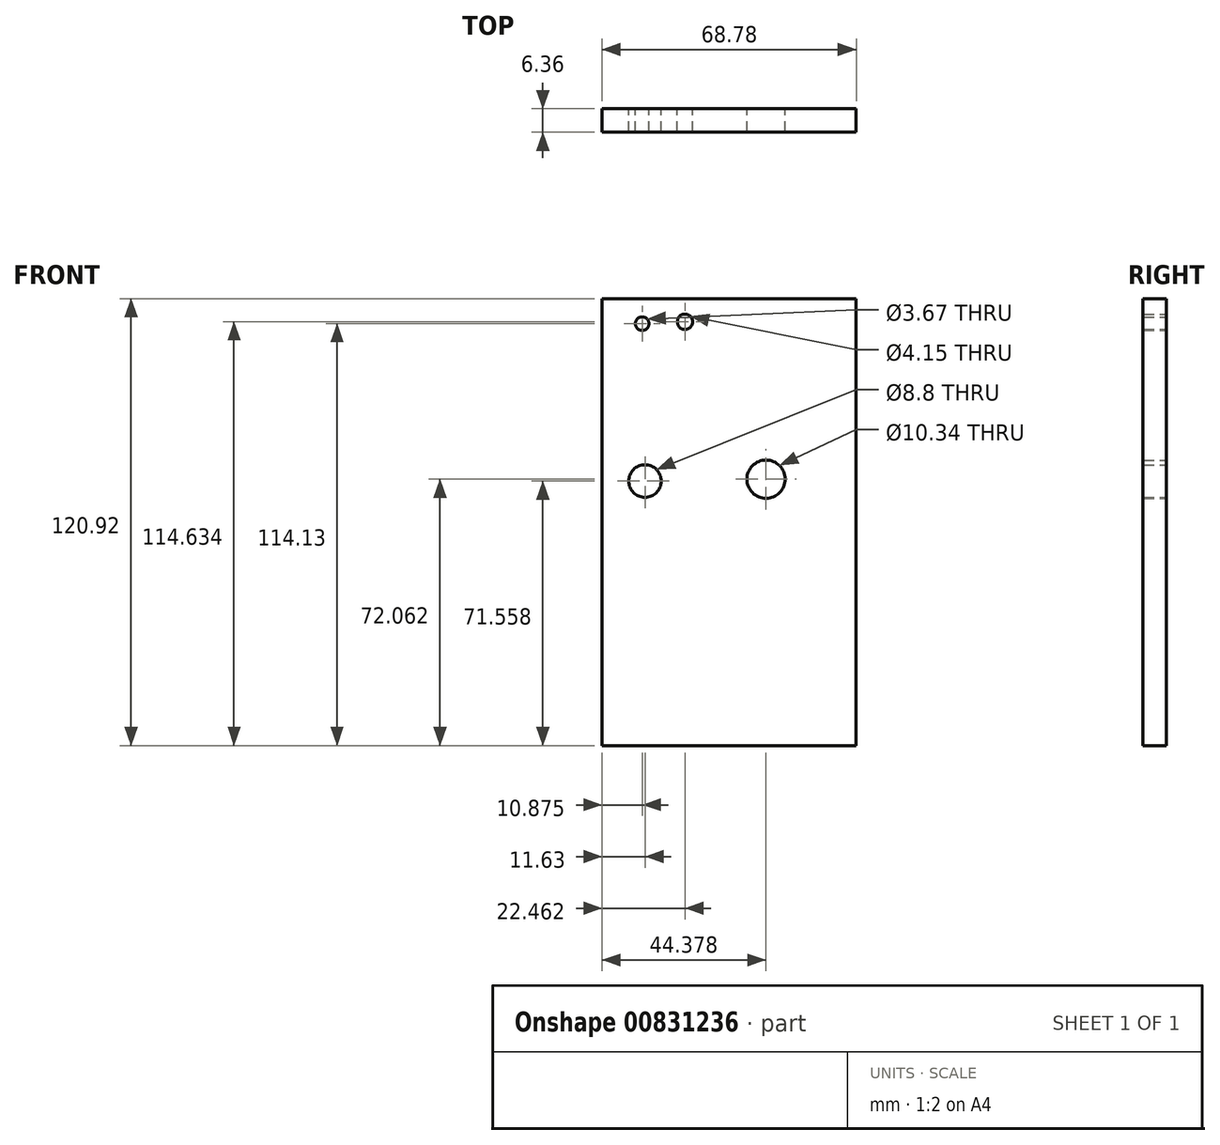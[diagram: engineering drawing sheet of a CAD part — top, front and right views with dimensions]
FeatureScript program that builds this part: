
annotation { "Feature Type Name" : "Feature", "Feature Type Description" : "" }
export const myFeature = defineFeature(function(context is Context, id is Id, definition is map)
    precondition{}
    {
        {
            var Q0;
            Q0=qCreatedBy(makeId("Front.planeOp"),FACE);
            var sketch = newSketch(context, id + "F0", { "sketchPlane" : qUnion([Q0])});
            skLineSegment(sketch, "E0.bottom", {"start": v(-34.39, 58.32) * mm, "end": v(34.39, 58.32) * mm});
            skLineSegment(sketch, "E0.top", {"start": v(-34.39, -62.6) * mm, "end": v(34.39, -62.6) * mm});
            skLineSegment(sketch, "E0.left", {"start": v(-34.39, 58.32) * mm, "end": v(-34.39, -62.6) * mm});
            skLineSegment(sketch, "E0.right", {"start": v(34.39, 58.32) * mm, "end": v(34.39, -62.6) * mm});
            skPoint(sketch, "E0.middle", {"position": v(0, -2.14) * mm});
            skCircle(sketch, "E1", {"center": v(-23.52, 51.53) * mm, "radius": 1.83 * mm});
            skCircle(sketch, "E2", {"center": v(-11.93, 52.03) * mm, "radius": 2.08 * mm});
            skCircle(sketch, "E3", {"center": v(-22.76, 8.96) * mm, "radius": 4.4 * mm});
            skCircle(sketch, "E4", {"center": v(9.99, 9.46) * mm, "radius": 5.17 * mm});
            skSolve(sketch);
        }
        {
            var Q0;
            Q0=makeQuery(id+"F0.imprint","IMPRINT",FACE,{"disambiguationData":[TD([[makeQuery(id+"F0.imprint","IMPRINT",EDGE,{"derivedFrom":sQuery(id+"F0.wireOp",EDGE,"E0.bottom")}),-1.0]])]});
            extrude(context, id + "F1", {"entities" : qUnion([Q0]), "endBound" : BoundingType.SYMMETRIC, "depth" : 6.35 * mm, "offsetDistance" : 25.4 * mm});
        }
    });
